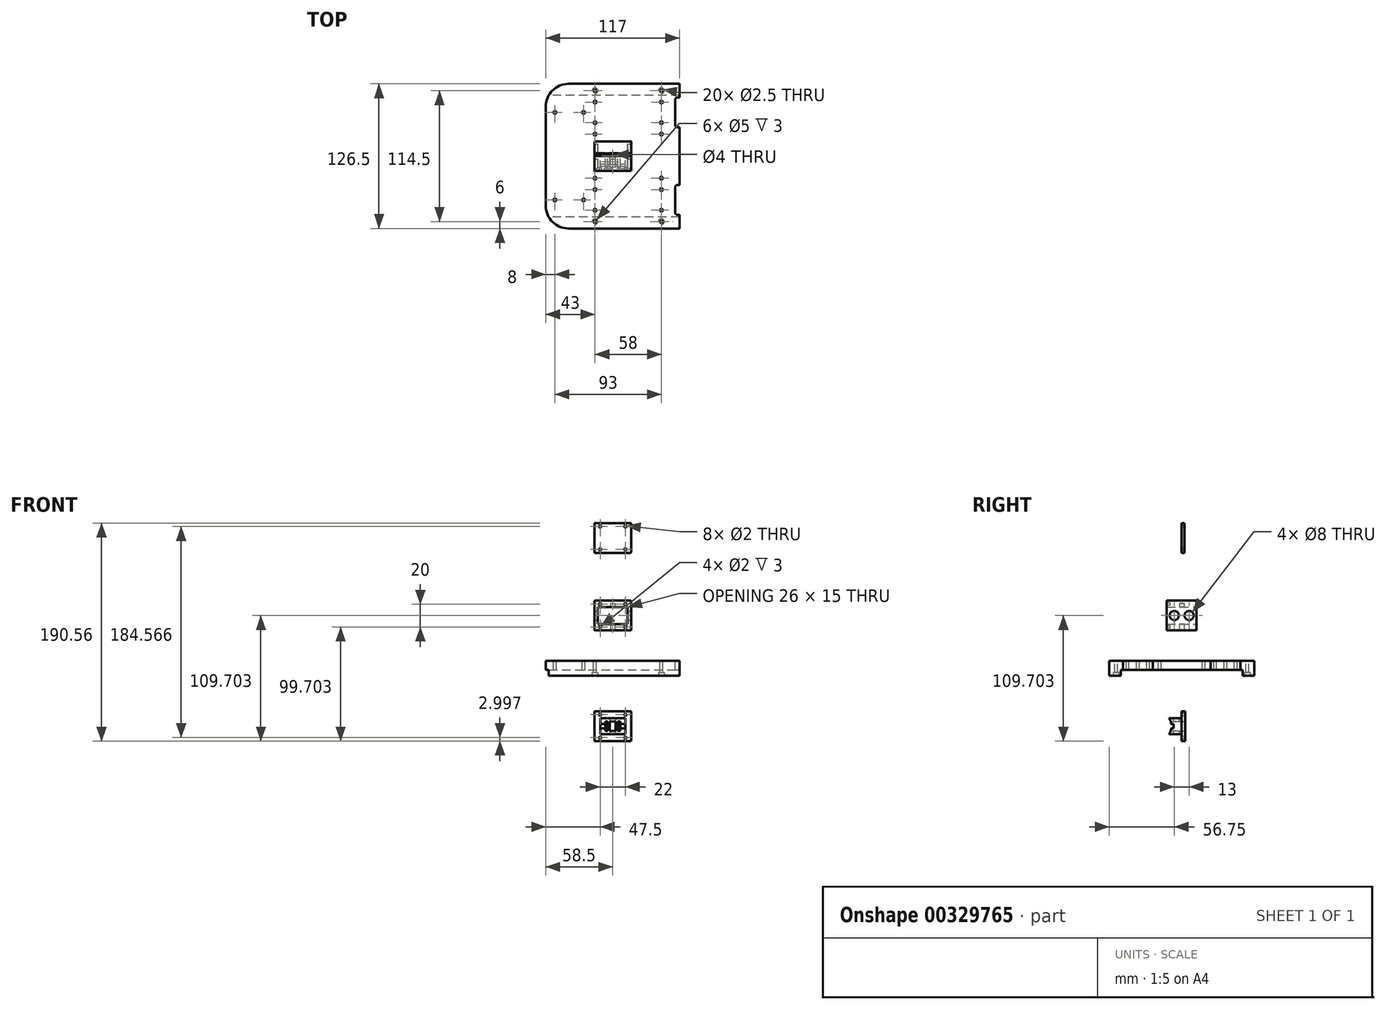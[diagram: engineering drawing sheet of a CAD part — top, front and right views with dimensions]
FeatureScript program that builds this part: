
annotation { "Feature Type Name" : "Feature", "Feature Type Description" : "" }
export const myFeature = defineFeature(function(context is Context, id is Id, definition is map)
    precondition{}
    {
        {
            var Q0;
            Q0=qCreatedBy(makeId("Top.planeOp"),FACE);
            var sketch = newSketch(context, id + "F0", { "sketchPlane" : qUnion([Q0])});
            skLineSegment(sketch, "E0.bottom", {"start": v(58.5, 63.25) * mm, "end": v(-38.5, 63.25) * mm});
            skLineSegment(sketch, "E0.top", {"start": v(58.5, -63.25) * mm, "end": v(-38.5, -63.25) * mm});
            skLineSegment(sketch, "E0.left", {"start": v(58.5, 63.25) * mm, "end": v(58.5, 51.25) * mm});
            skLineSegment(sketch, "E0.right", {"start": v(-58.5, 43.25) * mm, "end": v(-58.5, -43.25) * mm});
            skPoint(sketch, "E0.middle", {"position": v(0, 0) * mm});
            skPoint(sketch, "E1.visualSharp", {"position": v(-58.5, 63.25) * mm});
            skArc(sketch, "E1.filletArc", {"start": v(-38.5, 63.25) * mm, "mid": v(-52.64, 57.4) * mm, "end": v(-58.5, 43.25) * mm});
            skPoint(sketch, "E2.visualSharp", {"position": v(-58.5, -63.25) * mm});
            skArc(sketch, "E2.filletArc", {"start": v(-58.5, -43.25) * mm, "mid": v(-52.64, -57.4) * mm, "end": v(-38.5, -63.25) * mm});
            skLineSegment(sketch, "E3", {"start": v(-67.42, 0) * mm, "end": v(70.07, 0) * mm, "construction": true});
            skLineSegment(sketch, "E4", {"start": v(58.5, 51.25) * mm, "end": v(56.5, 51.25) * mm});
            skLineSegment(sketch, "E5", {"start": v(54.5, 49.25) * mm, "end": v(54.5, 27.25) * mm});
            skLineSegment(sketch, "E6", {"start": v(56.5, 25.25) * mm, "end": v(58.5, 25.25) * mm});
            skLineSegment(sketch, "E7.trimOffspring", {"start": v(58.5, 25.25) * mm, "end": v(58.5, -25.25) * mm});
            skPoint(sketch, "E8.visualSharp", {"position": v(54.5, 51.25) * mm});
            skArc(sketch, "E8.filletArc", {"start": v(56.5, 51.25) * mm, "mid": v(55.09, 50.66) * mm, "end": v(54.5, 49.25) * mm});
            skPoint(sketch, "E9.visualSharp", {"position": v(54.5, 25.25) * mm});
            skArc(sketch, "E9.filletArc", {"start": v(54.5, 27.25) * mm, "mid": v(55.09, 25.84) * mm, "end": v(56.5, 25.25) * mm});
            skCircle(sketch, "E10", {"center": v(-15.5, 19.25) * mm, "radius": 1.25 * mm});
            skCircle(sketch, "E11", {"center": v(-15.5, 29.25) * mm, "radius": 1.25 * mm});
            skCircle(sketch, "E12", {"center": v(-15.5, 47.25) * mm, "radius": 1.25 * mm});
            skCircle(sketch, "E13", {"center": v(-15.5, 57.25) * mm, "radius": 1.25 * mm});
            skCircle(sketch, "E14", {"center": v(42.5, 19.25) * mm, "radius": 1.25 * mm});
            skCircle(sketch, "E15", {"center": v(42.5, 29.25) * mm, "radius": 1.25 * mm});
            skCircle(sketch, "E16", {"center": v(42.5, 47.25) * mm, "radius": 1.25 * mm});
            skCircle(sketch, "E17", {"center": v(42.5, 57.25) * mm, "radius": 1.25 * mm});
            skCircle(sketch, "E18", {"center": v(-25.5, 38.25) * mm, "radius": 1.25 * mm});
            skCircle(sketch, "E19", {"center": v(-50.5, 38.25) * mm, "radius": 1.25 * mm});
            skCircle(sketch, "E20.MirrorC", {"center": v(42.5, -29.25) * mm, "radius": 1.25 * mm});
            skCircle(sketch, "E21.MirrorC", {"center": v(42.5, -57.25) * mm, "radius": 1.25 * mm});
            skCircle(sketch, "E22.MirrorC", {"center": v(42.5, -47.25) * mm, "radius": 1.25 * mm});
            skCircle(sketch, "E23.MirrorC", {"center": v(42.5, -19.25) * mm, "radius": 1.25 * mm});
            skCircle(sketch, "E24.MirrorC", {"center": v(-15.5, -57.25) * mm, "radius": 1.25 * mm});
            skCircle(sketch, "E25.MirrorC", {"center": v(-15.5, -19.25) * mm, "radius": 1.25 * mm});
            skCircle(sketch, "E26.MirrorC", {"center": v(-15.5, -29.25) * mm, "radius": 1.25 * mm});
            skCircle(sketch, "E27.MirrorC", {"center": v(-15.5, -47.25) * mm, "radius": 1.25 * mm});
            skCircle(sketch, "E28.MirrorC", {"center": v(-50.5, -38.25) * mm, "radius": 1.25 * mm});
            skCircle(sketch, "E29.MirrorC", {"center": v(-25.5, -38.25) * mm, "radius": 1.25 * mm});
            skLineSegment(sketch, "E30.MirrorCS", {"start": v(58.5, -51.25) * mm, "end": v(56.5, -51.25) * mm});
            skArc(sketch, "E31.MirrorCS", {"start": v(54.5, -27.25) * mm, "mid": v(55.09, -25.84) * mm, "end": v(56.5, -25.25) * mm});
            skArc(sketch, "E32.MirrorCS", {"start": v(56.5, -51.25) * mm, "mid": v(55.09, -50.66) * mm, "end": v(54.5, -49.25) * mm});
            skLineSegment(sketch, "E33.MirrorCS", {"start": v(56.5, -25.25) * mm, "end": v(58.5, -25.25) * mm});
            skLineSegment(sketch, "E34.MirrorCS", {"start": v(54.5, -49.25) * mm, "end": v(54.5, -27.25) * mm});
            skPoint(sketch, "E35.MirrorP", {"position": v(54.5, -51.25) * mm});
            skPoint(sketch, "E36.MirrorP", {"position": v(54.5, -25.25) * mm});
            skLineSegment(sketch, "E37.trimOffspring", {"start": v(58.5, -51.25) * mm, "end": v(58.5, -63.25) * mm});
            skSolve(sketch);
        }
        {
            var Q0;
            Q0 = qSketchRegion(id + "F0", true);
            extrude(context, id + "F1", {"entities" : qUnion([Q0]), "oppositeDirection" : true, "depth" : 13 * mm});
        }
        {
            var Q0;
            Q0=qCreatedBy(makeId("Right.planeOp"),FACE);
            var sketch = newSketch(context, id + "F2", { "sketchPlane" : qUnion([Q0])});
            skLineSegment(sketch, "E38.bottom", {"start": v(-53.25, -19.83) * mm, "end": v(53.25, -19.83) * mm});
            skLineSegment(sketch, "E38.top", {"start": v(-53.25, -8) * mm, "end": v(53.25, -8) * mm});
            skLineSegment(sketch, "E38.left", {"start": v(-53.25, -19.83) * mm, "end": v(-53.25, -8) * mm});
            skLineSegment(sketch, "E38.right", {"start": v(53.25, -19.83) * mm, "end": v(53.25, -8) * mm});
            skSolve(sketch);
        }
        {
            var Q0;
            Q0 = qSketchRegion(id + "F2", true);
            extrude(context, id + "F3", {"entities" : qUnion([Q0]), "operationType" : NewBodyOperationType.REMOVE, "oppositeDirection" : true, "depth" : 120 * mm, "symmetric" : true});
        }
        {
            var Q0;
            {var subQ0=sQuery(id+"F0.wireOp",EDGE,"E21.MirrorC");var subQ1=sQuery(id+"F0.wireOp",EDGE,"E0.top");var subQ2=sQuery(id+"F0.wireOp",EDGE,"E2.filletArc");var subQ3=sQuery(id+"F0.wireOp",EDGE,"E24.MirrorC");var subQ4=sQuery(id+"F0.wireOp",EDGE,"E37.trimOffspring");Q0=makeQuery(id+"F3.boolean.opBoolean","SPLIT",FACE,{"disambiguationData":[TD([makeQuery(id+"F1.opExtrude","SWEPT_FACE",FACE,{"disambiguationData":[OSD([subQ1])]})])],"derivedFrom":makeQuery(id+"F1.opExtrude","CAP_FACE",FACE,{"disambiguationData":[OSD([sQuery(id+"F0.wireOp",EDGE,"E0.bottom"),subQ1,sQuery(id+"F0.wireOp",EDGE,"E0.left"),sQuery(id+"F0.wireOp",EDGE,"E0.right"),sQuery(id+"F0.wireOp",EDGE,"E1.filletArc"),subQ2,sQuery(id+"F0.wireOp",EDGE,"E4"),sQuery(id+"F0.wireOp",EDGE,"E5"),sQuery(id+"F0.wireOp",EDGE,"E6"),sQuery(id+"F0.wireOp",EDGE,"E7.trimOffspring"),sQuery(id+"F0.wireOp",EDGE,"E8.filletArc"),sQuery(id+"F0.wireOp",EDGE,"E9.filletArc"),sQuery(id+"F0.wireOp",EDGE,"E10"),sQuery(id+"F0.wireOp",EDGE,"E11"),sQuery(id+"F0.wireOp",EDGE,"E12"),sQuery(id+"F0.wireOp",EDGE,"E13"),sQuery(id+"F0.wireOp",EDGE,"E14"),sQuery(id+"F0.wireOp",EDGE,"E15"),sQuery(id+"F0.wireOp",EDGE,"E16"),sQuery(id+"F0.wireOp",EDGE,"E17"),sQuery(id+"F0.wireOp",EDGE,"E18"),sQuery(id+"F0.wireOp",EDGE,"E19"),sQuery(id+"F0.wireOp",EDGE,"E20.MirrorC"),subQ0,sQuery(id+"F0.wireOp",EDGE,"E22.MirrorC"),sQuery(id+"F0.wireOp",EDGE,"E23.MirrorC"),subQ3,sQuery(id+"F0.wireOp",EDGE,"E25.MirrorC"),sQuery(id+"F0.wireOp",EDGE,"E26.MirrorC"),sQuery(id+"F0.wireOp",EDGE,"E27.MirrorC"),sQuery(id+"F0.wireOp",EDGE,"E28.MirrorC"),sQuery(id+"F0.wireOp",EDGE,"E29.MirrorC"),sQuery(id+"F0.wireOp",EDGE,"E30.MirrorCS"),sQuery(id+"F0.wireOp",EDGE,"E31.MirrorCS"),sQuery(id+"F0.wireOp",EDGE,"E32.MirrorCS"),sQuery(id+"F0.wireOp",EDGE,"E33.MirrorCS"),sQuery(id+"F0.wireOp",EDGE,"E34.MirrorCS"),subQ4])],"isStart":false})});}
            var sketch = newSketch(context, id + "F4", { "sketchPlane" : qUnion([Q0])});
            skCircle(sketch, "E39", {"center": v(-15.5, 57.25) * mm, "radius": 2.5 * mm});
            skCircle(sketch, "E40", {"center": v(42.5, 57.25) * mm, "radius": 2.5 * mm});
            skSolve(sketch);
        }
        {
            var Q0;
            Q0 = qSketchRegion(id + "F4", true);
            extrude(context, id + "F5", {"entities" : qUnion([Q0]), "operationType" : NewBodyOperationType.REMOVE, "oppositeDirection" : true, "depth" : 3 * mm});
        }
        {
            var Q0;
            {var subQ0=sQuery(id+"F0.wireOp",EDGE,"E13");var subQ1=sQuery(id+"F0.wireOp",EDGE,"E1.filletArc");var subQ2=sQuery(id+"F0.wireOp",EDGE,"E0.left");var subQ3=sQuery(id+"F0.wireOp",EDGE,"E0.bottom");var subQ4=sQuery(id+"F0.wireOp",EDGE,"E17");Q0=makeQuery(id+"F3.boolean.opBoolean","SPLIT",FACE,{"disambiguationData":[TD([makeQuery(id+"F1.opExtrude","SWEPT_FACE",FACE,{"disambiguationData":[OSD([subQ3])]})])],"derivedFrom":makeQuery(id+"F1.opExtrude","CAP_FACE",FACE,{"disambiguationData":[OSD([subQ3,sQuery(id+"F0.wireOp",EDGE,"E0.top"),subQ2,sQuery(id+"F0.wireOp",EDGE,"E0.right"),subQ1,sQuery(id+"F0.wireOp",EDGE,"E2.filletArc"),sQuery(id+"F0.wireOp",EDGE,"E4"),sQuery(id+"F0.wireOp",EDGE,"E5"),sQuery(id+"F0.wireOp",EDGE,"E6"),sQuery(id+"F0.wireOp",EDGE,"E7.trimOffspring"),sQuery(id+"F0.wireOp",EDGE,"E8.filletArc"),sQuery(id+"F0.wireOp",EDGE,"E9.filletArc"),sQuery(id+"F0.wireOp",EDGE,"E10"),sQuery(id+"F0.wireOp",EDGE,"E11"),sQuery(id+"F0.wireOp",EDGE,"E12"),subQ0,sQuery(id+"F0.wireOp",EDGE,"E14"),sQuery(id+"F0.wireOp",EDGE,"E15"),sQuery(id+"F0.wireOp",EDGE,"E16"),subQ4,sQuery(id+"F0.wireOp",EDGE,"E18"),sQuery(id+"F0.wireOp",EDGE,"E19"),sQuery(id+"F0.wireOp",EDGE,"E20.MirrorC"),sQuery(id+"F0.wireOp",EDGE,"E21.MirrorC"),sQuery(id+"F0.wireOp",EDGE,"E22.MirrorC"),sQuery(id+"F0.wireOp",EDGE,"E23.MirrorC"),sQuery(id+"F0.wireOp",EDGE,"E24.MirrorC"),sQuery(id+"F0.wireOp",EDGE,"E25.MirrorC"),sQuery(id+"F0.wireOp",EDGE,"E26.MirrorC"),sQuery(id+"F0.wireOp",EDGE,"E27.MirrorC"),sQuery(id+"F0.wireOp",EDGE,"E28.MirrorC"),sQuery(id+"F0.wireOp",EDGE,"E29.MirrorC"),sQuery(id+"F0.wireOp",EDGE,"E30.MirrorCS"),sQuery(id+"F0.wireOp",EDGE,"E31.MirrorCS"),sQuery(id+"F0.wireOp",EDGE,"E32.MirrorCS"),sQuery(id+"F0.wireOp",EDGE,"E33.MirrorCS"),sQuery(id+"F0.wireOp",EDGE,"E34.MirrorCS"),sQuery(id+"F0.wireOp",EDGE,"E37.trimOffspring")])],"isStart":false})});}
            var sketch = newSketch(context, id + "F6", { "sketchPlane" : qUnion([Q0])});
            skCircle(sketch, "E41", {"center": v(-15.5, -57.25) * mm, "radius": 2.5 * mm});
            skCircle(sketch, "E42", {"center": v(42.5, -57.25) * mm, "radius": 2.5 * mm});
            skSolve(sketch);
        }
        {
            var Q0;
            Q0 = qSketchRegion(id + "F6", true);
            extrude(context, id + "F7", {"entities" : qUnion([Q0]), "operationType" : NewBodyOperationType.REMOVE, "oppositeDirection" : true, "depth" : 3 * mm});
        }
        {
            var Q0;
            Q0=qCreatedBy(makeId("Front.planeOp"),FACE);
            var sketch = newSketch(context, id + "F8", { "sketchPlane" : qUnion([Q0])});
            skLineSegment(sketch, "E43.bottom", {"start": v(16, 52.6) * mm, "end": v(-16, 52.6) * mm});
            skLineSegment(sketch, "E43.top", {"start": v(16, 26.6) * mm, "end": v(-16, 26.6) * mm});
            skLineSegment(sketch, "E43.left", {"start": v(16, 52.6) * mm, "end": v(16, 26.6) * mm});
            skLineSegment(sketch, "E43.right", {"start": v(-16, 52.6) * mm, "end": v(-16, 26.6) * mm});
            skPoint(sketch, "E43.middle", {"position": v(0, 39.6) * mm});
            skLineSegment(sketch, "E44.bottom", {"start": v(13, 47.1) * mm, "end": v(-13, 47.1) * mm});
            skLineSegment(sketch, "E44.top", {"start": v(13, 32.1) * mm, "end": v(-13, 32.1) * mm});
            skLineSegment(sketch, "E44.left", {"start": v(13, 47.1) * mm, "end": v(13, 32.1) * mm});
            skLineSegment(sketch, "E44.right", {"start": v(-13, 47.1) * mm, "end": v(-13, 32.1) * mm});
            skSolve(sketch);
        }
        {
            var Q0;
            Q0 = qSketchRegion(id + "F8", true);
            extrude(context, id + "F9", {"entities" : qUnion([Q0]), "depth" : 26 * mm, "symmetric" : true});
        }
        {
            var Q0;
            Q0=makeQuery(id+"F9.opExtrude","CAP_FACE",FACE,{"disambiguationData":[OSD([sQuery(id+"F8.wireOp",EDGE,"E43.bottom"),sQuery(id+"F8.wireOp",EDGE,"E43.top"),sQuery(id+"F8.wireOp",EDGE,"E43.left"),sQuery(id+"F8.wireOp",EDGE,"E43.right"),sQuery(id+"F8.wireOp",EDGE,"E44.bottom"),sQuery(id+"F8.wireOp",EDGE,"E44.top"),sQuery(id+"F8.wireOp",EDGE,"E44.left"),sQuery(id+"F8.wireOp",EDGE,"E44.right")])],"isStart":false});
            var sketch = newSketch(context, id + "F10", { "sketchPlane" : qUnion([Q0])});
            skCircle(sketch, "E45", {"center": v(-11, 49.6) * mm, "radius": 1 * mm});
            skCircle(sketch, "E46", {"center": v(11, 49.6) * mm, "radius": 1 * mm});
            skCircle(sketch, "E47", {"center": v(-11, 29.6) * mm, "radius": 1 * mm});
            skCircle(sketch, "E48", {"center": v(11, 29.6) * mm, "radius": 1 * mm});
            skSolve(sketch);
        }
        {
            var Q0;
            Q0 = qSketchRegion(id + "F10", true);
            extrude(context, id + "F11", {"entities" : qUnion([Q0]), "operationType" : NewBodyOperationType.REMOVE, "oppositeDirection" : true, "depth" : 3 * mm});
        }
        {
            var Q0;
            Q0=makeQuery(id+"F9.opExtrude","SWEPT_FACE",FACE,{"disambiguationData":[OSD([sQuery(id+"F8.wireOp",EDGE,"E43.left")])]});
            var sketch = newSketch(context, id + "F12", { "sketchPlane" : qUnion([Q0])});
            skCircle(sketch, "E49", {"center": v(-6.5, 39.6) * mm, "radius": 4 * mm});
            skCircle(sketch, "E50", {"center": v(6.5, 39.6) * mm, "radius": 4 * mm});
            skSolve(sketch);
        }
        {
            var Q0;
            Q0 = qSketchRegion(id + "F12", true);
            extrude(context, id + "F13", {"entities" : qUnion([Q0]), "operationType" : NewBodyOperationType.REMOVE, "oppositeDirection" : true, "depth" : 35 * mm});
        }
        {
            var Q0;
            Q0=makeQuery(id+"F9.opExtrude","SWEPT_FACE",FACE,{"disambiguationData":[OSD([sQuery(id+"F8.wireOp",EDGE,"E44.bottom")])]});
            var sketch = newSketch(context, id + "F14", { "sketchPlane" : qUnion([Q0])});
            skCircle(sketch, "E51", {"center": v(0, 0) * mm, "radius": 2 * mm});
            skSolve(sketch);
        }
        {
            var Q0;
            Q0 = qSketchRegion(id + "F14", true);
            extrude(context, id + "F15", {"entities" : qUnion([Q0]), "operationType" : NewBodyOperationType.REMOVE, "oppositeDirection" : true, "depth" : 3 * mm});
        }
        {
            var Q0;
            Q0=makeQuery(id+"F9.opExtrude","SWEPT_FACE",FACE,{"disambiguationData":[OSD([sQuery(id+"F8.wireOp",EDGE,"E43.top")])]});
            var sketch = newSketch(context, id + "F16", { "sketchPlane" : qUnion([Q0])});
            skCircle(sketch, "E52", {"center": v(0, 0) * mm, "radius": 2 * mm});
            skSolve(sketch);
        }
        {
            var Q0;
            Q0 = qSketchRegion(id + "F16", true);
            extrude(context, id + "F17", {"entities" : qUnion([Q0]), "operationType" : NewBodyOperationType.REMOVE, "oppositeDirection" : true, "depth" : 12 * mm});
        }
        {
            var Q0;
            Q0=makeQuery(id+"F9.opExtrude","SWEPT_EDGE",EDGE,{"disambiguationData":[OSD([sQuery(id+"F8.wireOp",EDGE,"E43.bottom"),sQuery(id+"F8.wireOp",EDGE,"E43.left")])]});
            var Q1;
            Q1=makeQuery(id+"F9.opExtrude","SWEPT_EDGE",EDGE,{"disambiguationData":[OSD([sQuery(id+"F8.wireOp",EDGE,"E43.bottom"),sQuery(id+"F8.wireOp",EDGE,"E43.right")])]});
            var Q2;
            Q2=makeQuery(id+"F9.opExtrude","SWEPT_EDGE",EDGE,{"disambiguationData":[OSD([sQuery(id+"F8.wireOp",EDGE,"E43.top"),sQuery(id+"F8.wireOp",EDGE,"E43.left")])]});
            var Q3;
            Q3=makeQuery(id+"F9.opExtrude","SWEPT_EDGE",EDGE,{"disambiguationData":[OSD([sQuery(id+"F8.wireOp",EDGE,"E44.top"),sQuery(id+"F8.wireOp",EDGE,"E44.right")])]});
            var Q4;
            Q4=makeQuery(id+"F9.opExtrude","SWEPT_EDGE",EDGE,{"disambiguationData":[OSD([sQuery(id+"F8.wireOp",EDGE,"E43.top"),sQuery(id+"F8.wireOp",EDGE,"E43.right")])]});
            fillet(context, id + "F18", {"entities" : qUnion([Q0, Q1, Q2, Q3, Q4]), "radius" : .5 * mm, "tangentPropagation" : true, "allowEdgeOverflow" : false});
        }
        {
            var Q0;
            Q0=qCreatedBy(makeId("Front.planeOp"),FACE);
            var sketch = newSketch(context, id + "F19", { "sketchPlane" : qUnion([Q0])});
            skLineSegment(sketch, "E53.bottom", {"start": v(16, 120.46) * mm, "end": v(-16, 120.46) * mm});
            skLineSegment(sketch, "E53.top", {"start": v(16, 94.46) * mm, "end": v(-16, 94.46) * mm});
            skLineSegment(sketch, "E53.left", {"start": v(16, 120.46) * mm, "end": v(16, 94.46) * mm});
            skLineSegment(sketch, "E53.right", {"start": v(-16, 120.46) * mm, "end": v(-16, 94.46) * mm});
            skPoint(sketch, "E53.middle", {"position": v(0, 107.46) * mm});
            skCircle(sketch, "E54", {"center": v(-11, 117.46) * mm, "radius": 1 * mm});
            skCircle(sketch, "E55", {"center": v(11, 117.46) * mm, "radius": 1 * mm});
            skCircle(sketch, "E56", {"center": v(11, 97.46) * mm, "radius": 1 * mm});
            skCircle(sketch, "E57", {"center": v(-11, 97.46) * mm, "radius": 1 * mm});
            skSolve(sketch);
        }
        {
            var Q0;
            Q0 = qSketchRegion(id + "F19", true);
            extrude(context, id + "F20", {"entities" : qUnion([Q0]), "oppositeDirection" : true, "depth" : 2.5 * mm});
        }
        {
            var Q0;
            Q0=makeQuery(id+"F20.opExtrude","SWEPT_EDGE",EDGE,{"disambiguationData":[OSD([sQuery(id+"F19.wireOp",EDGE,"E53.bottom"),sQuery(id+"F19.wireOp",EDGE,"E53.left")])]});
            var Q1;
            Q1=makeQuery(id+"F20.opExtrude","SWEPT_EDGE",EDGE,{"disambiguationData":[OSD([sQuery(id+"F19.wireOp",EDGE,"E53.top"),sQuery(id+"F19.wireOp",EDGE,"E53.left")])]});
            var Q2;
            Q2=makeQuery(id+"F20.opExtrude","SWEPT_EDGE",EDGE,{"disambiguationData":[OSD([sQuery(id+"F19.wireOp",EDGE,"E53.bottom"),sQuery(id+"F19.wireOp",EDGE,"E53.right")])]});
            var Q3;
            Q3=makeQuery(id+"F20.opExtrude","SWEPT_EDGE",EDGE,{"disambiguationData":[OSD([sQuery(id+"F19.wireOp",EDGE,"E53.top"),sQuery(id+"F19.wireOp",EDGE,"E53.right")])]});
            fillet(context, id + "F21", {"entities" : qUnion([Q0, Q1, Q2, Q3]), "radius" : 0.5 * mm, "tangentPropagation" : true, "allowEdgeOverflow" : false});
        }
        {
            var Q0;
            Q0=qCreatedBy(makeId("Front.planeOp"),FACE);
            var sketch = newSketch(context, id + "F22", { "sketchPlane" : qUnion([Q0])});
            skLineSegment(sketch, "E58.bottom", {"start": v(16, -44.1) * mm, "end": v(-16, -44.1) * mm});
            skLineSegment(sketch, "E58.top", {"start": v(16, -70.1) * mm, "end": v(-16, -70.1) * mm});
            skLineSegment(sketch, "E58.left", {"start": v(16, -44.1) * mm, "end": v(16, -70.1) * mm});
            skLineSegment(sketch, "E58.right", {"start": v(-16, -44.1) * mm, "end": v(-16, -70.1) * mm});
            skPoint(sketch, "E58.middle", {"position": v(0, -57.1) * mm});
            skCircle(sketch, "E59", {"center": v(-11, -47.1) * mm, "radius": 1 * mm});
            skCircle(sketch, "E60", {"center": v(11, -47.1) * mm, "radius": 1 * mm});
            skCircle(sketch, "E61", {"center": v(11, -67.1) * mm, "radius": 1 * mm});
            skCircle(sketch, "E62", {"center": v(-11, -67.1) * mm, "radius": 1 * mm});
            skSolve(sketch);
        }
        {
            var Q0;
            Q0 = qSketchRegion(id + "F22", true);
            extrude(context, id + "F23", {"entities" : qUnion([Q0]), "oppositeDirection" : true, "depth" : 3 * mm});
        }
        {
            var Q0;
            Q0=makeQuery(id+"F23.opExtrude","CAP_FACE",FACE,{"disambiguationData":[OSD([sQuery(id+"F22.wireOp",EDGE,"E58.bottom"),sQuery(id+"F22.wireOp",EDGE,"E58.top"),sQuery(id+"F22.wireOp",EDGE,"E58.left"),sQuery(id+"F22.wireOp",EDGE,"E58.right"),sQuery(id+"F22.wireOp",EDGE,"E59"),sQuery(id+"F22.wireOp",EDGE,"E60"),sQuery(id+"F22.wireOp",EDGE,"E61"),sQuery(id+"F22.wireOp",EDGE,"E62")])],"isStart":true});
            var sketch = newSketch(context, id + "F24", { "sketchPlane" : qUnion([Q0])});
            skLineSegment(sketch, "E63.bottom", {"start": v(11, -50.1) * mm, "end": v(-11, -50.1) * mm});
            skLineSegment(sketch, "E63.top", {"start": v(11, -64.1) * mm, "end": v(-11, -64.1) * mm});
            skLineSegment(sketch, "E63.left", {"start": v(11, -50.1) * mm, "end": v(11, -64.1) * mm});
            skLineSegment(sketch, "E63.right", {"start": v(-11, -50.1) * mm, "end": v(-11, -64.1) * mm});
            skPoint(sketch, "E63.middle", {"position": v(0, -57.1) * mm});
            skSolve(sketch);
        }
        {
            var Q0;
            Q0 = qSketchRegion(id + "F24", true);
            extrude(context, id + "F25", {"entities" : qUnion([Q0]), "operationType" : NewBodyOperationType.ADD, "depth" : 11 * mm});
        }
        {
            var Q0;
            Q0=makeQuery(id+"F25.opExtrude","SWEPT_FACE",FACE,{"disambiguationData":[OSD([sQuery(id+"F24.wireOp",EDGE,"E63.right")])]});
            var sketch = newSketch(context, id + "F26", { "sketchPlane" : qUnion([Q0])});
            skArc(sketch, "E64", {"start": v(11, -50.1) * mm, "mid": v(8.95, -57.1) * mm, "end": v(11, -64.1) * mm});
            skLineSegment(sketch, "E65", {"start": v(11, -50.1) * mm, "end": v(14.61, -50.1) * mm});
            skLineSegment(sketch, "E66", {"start": v(14.61, -50.1) * mm, "end": v(14.61, -64.1) * mm});
            skLineSegment(sketch, "E67", {"start": v(14.61, -64.1) * mm, "end": v(11, -64.1) * mm});
            skSolve(sketch);
        }
        {
            var Q0;
            Q0 = qSketchRegion(id + "F26", true);
            extrude(context, id + "F27", {"entities" : qUnion([Q0]), "operationType" : NewBodyOperationType.REMOVE, "oppositeDirection" : true, "depth" : 25 * mm});
        }
        {
            var Q0;
            Q0=makeQuery(id+"F25.opExtrude","SWEPT_FACE",FACE,{"disambiguationData":[OSD([sQuery(id+"F24.wireOp",EDGE,"E63.right")])]});
            var sketch = newSketch(context, id + "F28", { "sketchPlane" : qUnion([Q0])});
            skLineSegment(sketch, "E68.bottom", {"start": v(7, -55.1) * mm, "end": v(11.2, -55.1) * mm});
            skLineSegment(sketch, "E68.top", {"start": v(7, -59.1) * mm, "end": v(11.2, -59.1) * mm});
            skLineSegment(sketch, "E68.left", {"start": v(7, -55.1) * mm, "end": v(7, -59.1) * mm});
            skLineSegment(sketch, "E68.right", {"start": v(11.2, -55.1) * mm, "end": v(11.2, -59.1) * mm});
            skSolve(sketch);
        }
        {
            var Q0;
            Q0 = qSketchRegion(id + "F28", true);
            extrude(context, id + "F29", {"entities" : qUnion([Q0]), "operationType" : NewBodyOperationType.REMOVE, "oppositeDirection" : true, "depth" : 25 * mm});
        }
        {
            var Q0;
            Q0=makeQuery(id+"F23.opExtrude","CAP_FACE",FACE,{"disambiguationData":[OSD([sQuery(id+"F22.wireOp",EDGE,"E58.bottom"),sQuery(id+"F22.wireOp",EDGE,"E58.top"),sQuery(id+"F22.wireOp",EDGE,"E58.left"),sQuery(id+"F22.wireOp",EDGE,"E58.right"),sQuery(id+"F22.wireOp",EDGE,"E59"),sQuery(id+"F22.wireOp",EDGE,"E60"),sQuery(id+"F22.wireOp",EDGE,"E61"),sQuery(id+"F22.wireOp",EDGE,"E62")])],"isStart":false});
            var sketch = newSketch(context, id + "F30", { "sketchPlane" : qUnion([Q0])});
            skLineSegment(sketch, "E69.bottom", {"start": v(2.5, -53.1) * mm, "end": v(-2.5, -53.1) * mm});
            skLineSegment(sketch, "E69.top", {"start": v(2.5, -61.1) * mm, "end": v(-2.5, -61.1) * mm});
            skLineSegment(sketch, "E69.left", {"start": v(2.5, -53.1) * mm, "end": v(2.5, -61.1) * mm});
            skLineSegment(sketch, "E69.right", {"start": v(-2.5, -53.1) * mm, "end": v(-2.5, -61.1) * mm});
            skPoint(sketch, "E69.middle", {"position": v(0, -57.1) * mm});
            skLineSegment(sketch, "E70.bottom", {"start": v(-4.5, -53.1) * mm, "end": v(-6.5, -53.1) * mm});
            skLineSegment(sketch, "E70.top", {"start": v(-4.5, -61.1) * mm, "end": v(-6.5, -61.1) * mm});
            skLineSegment(sketch, "E70.left", {"start": v(-4.5, -53.1) * mm, "end": v(-4.5, -61.1) * mm});
            skLineSegment(sketch, "E70.right", {"start": v(-6.5, -53.1) * mm, "end": v(-6.5, -61.1) * mm});
            skPoint(sketch, "E70.middle", {"position": v(-5.5, -57.1) * mm});
            skLineSegment(sketch, "E71.bottom", {"start": v(6.5, -53.1) * mm, "end": v(4.5, -53.1) * mm});
            skLineSegment(sketch, "E71.top", {"start": v(6.5, -61.1) * mm, "end": v(4.5, -61.1) * mm});
            skLineSegment(sketch, "E71.left", {"start": v(6.5, -53.1) * mm, "end": v(6.5, -61.1) * mm});
            skLineSegment(sketch, "E71.right", {"start": v(4.5, -53.1) * mm, "end": v(4.5, -61.1) * mm});
            skPoint(sketch, "E71.middle", {"position": v(5.5, -57.1) * mm});
            skSolve(sketch);
        }
        {
            var Q0;
            Q0 = qSketchRegion(id + "F30", true);
            extrude(context, id + "F31", {"entities" : qUnion([Q0]), "operationType" : NewBodyOperationType.REMOVE, "oppositeDirection" : true, "depth" : 25 * mm});
        }
        {
            var Q0;
            Q0=makeQuery(id+"F25.opExtrude","SWEPT_FACE",FACE,{"disambiguationData":[OSD([sQuery(id+"F24.wireOp",EDGE,"E63.top")])]});
            var sketch = newSketch(context, id + "F32", { "sketchPlane" : qUnion([Q0])});
            skCircle(sketch, "E72", {"center": v(0, 5) * mm, "radius": 2.5 * mm});
            skSolve(sketch);
        }
        {
            var Q0;
            Q0 = qSketchRegion(id + "F32", true);
            extrude(context, id + "F33", {"entities" : qUnion([Q0]), "operationType" : NewBodyOperationType.REMOVE, "oppositeDirection" : true, "depth" : 25 * mm});
        }
        {
            var Q0;
            Q0=makeQuery(id+"F23.opExtrude","SWEPT_EDGE",EDGE,{"disambiguationData":[OSD([sQuery(id+"F22.wireOp",EDGE,"E58.top"),sQuery(id+"F22.wireOp",EDGE,"E58.left")])]});
            var Q1;
            Q1=makeQuery(id+"F23.opExtrude","SWEPT_EDGE",EDGE,{"disambiguationData":[OSD([sQuery(id+"F22.wireOp",EDGE,"E58.bottom"),sQuery(id+"F22.wireOp",EDGE,"E58.left")])]});
            var Q2;
            Q2=makeQuery(id+"F23.opExtrude","SWEPT_EDGE",EDGE,{"disambiguationData":[OSD([sQuery(id+"F22.wireOp",EDGE,"E58.top"),sQuery(id+"F22.wireOp",EDGE,"E58.right")])]});
            var Q3;
            Q3=makeQuery(id+"F23.opExtrude","SWEPT_EDGE",EDGE,{"disambiguationData":[OSD([sQuery(id+"F22.wireOp",EDGE,"E58.bottom"),sQuery(id+"F22.wireOp",EDGE,"E58.right")])]});
            fillet(context, id + "F34", {"entities" : qUnion([Q0, Q1, Q2, Q3]), "radius" : 0.5 * mm, "tangentPropagation" : true, "allowEdgeOverflow" : false});
        }
    });
